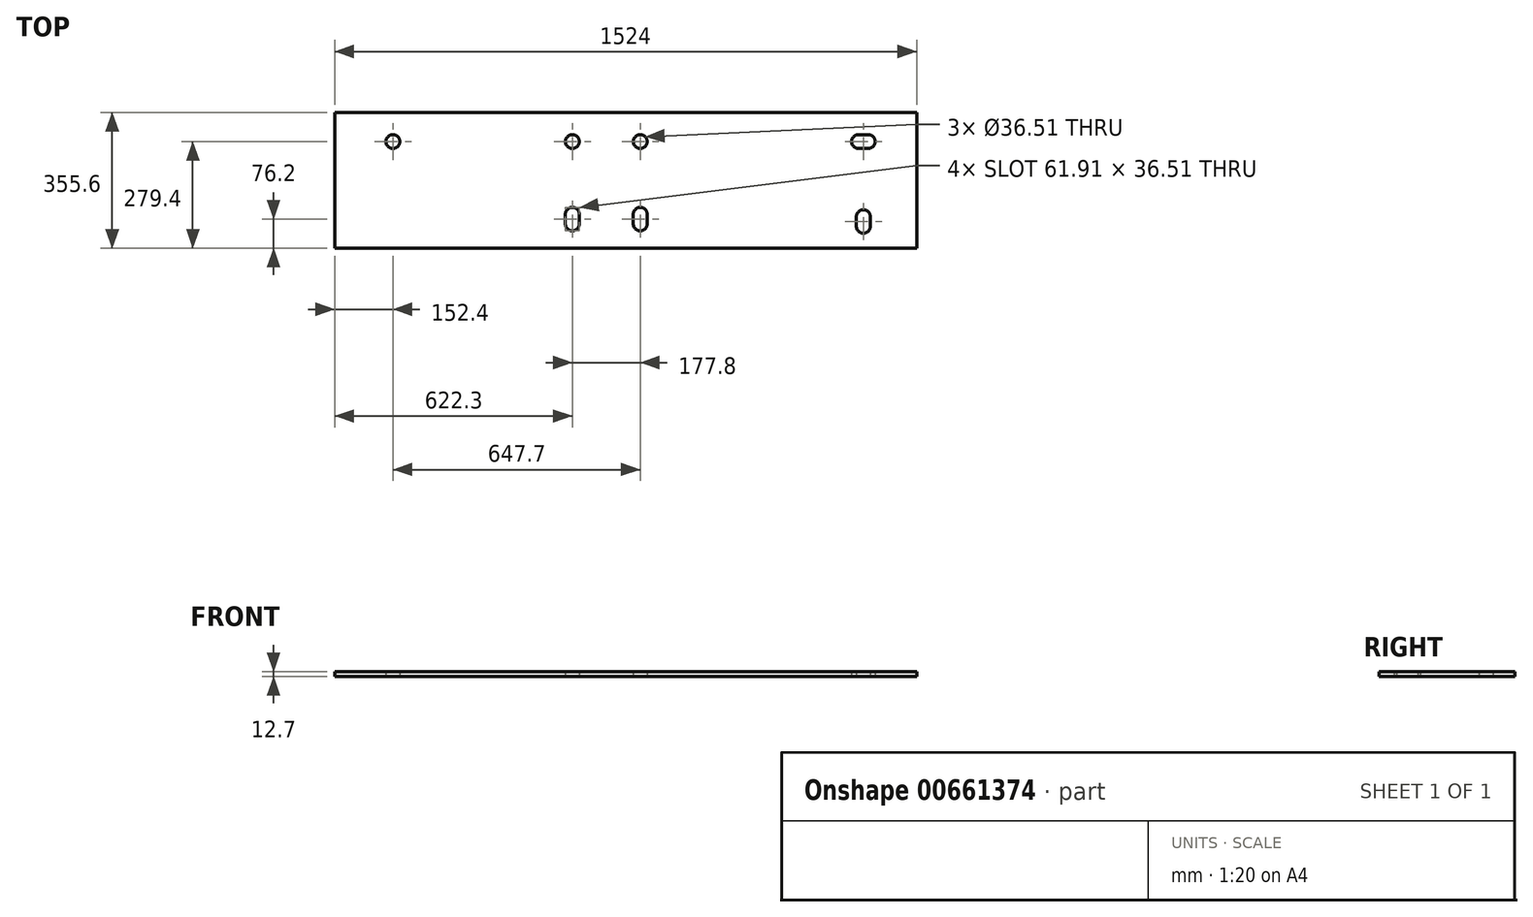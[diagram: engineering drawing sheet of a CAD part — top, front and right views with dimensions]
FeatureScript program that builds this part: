
annotation { "Feature Type Name" : "Feature", "Feature Type Description" : "" }
export const myFeature = defineFeature(function(context is Context, id is Id, definition is map)
    precondition{}
    {
        {
            var Q0;
            Q0=qCreatedBy(makeId("Top.planeOp"),FACE);
            var sketch = newSketch(context, id + "F0", { "sketchPlane" : qUnion([Q0])});
            skLineSegment(sketch, "E0.bottom", {"start": v(0, 0) * mm, "end": v(1524, 0) * mm});
            skLineSegment(sketch, "E0.top", {"start": v(0, 355.6) * mm, "end": v(1524, 355.6) * mm});
            skLineSegment(sketch, "E0.left", {"start": v(0, 0) * mm, "end": v(0, 355.6) * mm});
            skLineSegment(sketch, "E0.right", {"start": v(1524, 0) * mm, "end": v(1524, 355.6) * mm});
            skLineSegment(sketch, "E1", {"start": v(1397, 297.66) * mm, "end": v(1371.6, 297.66) * mm});
            skLineSegment(sketch, "E2", {"start": v(1371.6, 261.14) * mm, "end": v(1397, 261.14) * mm});
            skArc(sketch, "E3", {"start": v(1371.6, 297.66) * mm, "mid": v(1353.34, 279.4) * mm, "end": v(1371.6, 261.14) * mm});
            skArc(sketch, "E4", {"start": v(1397, 261.14) * mm, "mid": v(1415.26, 279.4) * mm, "end": v(1397, 297.66) * mm});
            skLineSegment(sketch, "E5", {"start": v(1366.04, 82.55) * mm, "end": v(1366.04, 57.15) * mm});
            skLineSegment(sketch, "E6", {"start": v(1402.56, 57.15) * mm, "end": v(1402.56, 82.55) * mm});
            skArc(sketch, "E7", {"start": v(1366.04, 57.15) * mm, "mid": v(1384.3, 38.9) * mm, "end": v(1402.56, 57.15) * mm});
            skArc(sketch, "E8", {"start": v(1402.56, 82.55) * mm, "mid": v(1384.3, 100.8) * mm, "end": v(1366.04, 82.55) * mm});
            skLineSegment(sketch, "E9", {"start": v(781.84, 88.9) * mm, "end": v(781.84, 63.5) * mm});
            skLineSegment(sketch, "E10", {"start": v(818.36, 63.5) * mm, "end": v(818.36, 88.9) * mm});
            skArc(sketch, "E11", {"start": v(781.84, 63.5) * mm, "mid": v(800.1, 45.24) * mm, "end": v(818.36, 63.5) * mm});
            skArc(sketch, "E12", {"start": v(818.36, 88.9) * mm, "mid": v(800.1, 107.16) * mm, "end": v(781.84, 88.9) * mm});
            skLineSegment(sketch, "E13", {"start": v(604.04, 88.9) * mm, "end": v(604.04, 63.5) * mm});
            skLineSegment(sketch, "E14", {"start": v(640.56, 63.5) * mm, "end": v(640.56, 88.9) * mm});
            skArc(sketch, "E15", {"start": v(604.04, 63.5) * mm, "mid": v(622.3, 45.24) * mm, "end": v(640.56, 63.5) * mm});
            skArc(sketch, "E16", {"start": v(640.56, 88.9) * mm, "mid": v(622.3, 107.16) * mm, "end": v(604.04, 88.9) * mm});
            skCircle(sketch, "E17", {"center": v(800.1, 279.4) * mm, "radius": 18.26 * mm});
            skCircle(sketch, "E18", {"center": v(622.3, 279.4) * mm, "radius": 18.26 * mm});
            skCircle(sketch, "E19", {"center": v(152.4, 279.4) * mm, "radius": 18.26 * mm});
            skPoint(sketch, "E20", {"position": v(1384.3, 297.66) * mm});
            skPoint(sketch, "E21", {"position": v(1402.56, 69.85) * mm});
            skPoint(sketch, "E22", {"position": v(640.56, 76.2) * mm});
            skSolve(sketch);
        }
        {
            var Q0;
            Q0 = qSketchRegion(id + "F0", true);
            extrude(context, id + "F1", {"entities" : qUnion([Q0]), "depth" : 12.7 * mm, "offsetDistance" : 25.4 * mm});
        }
    });
